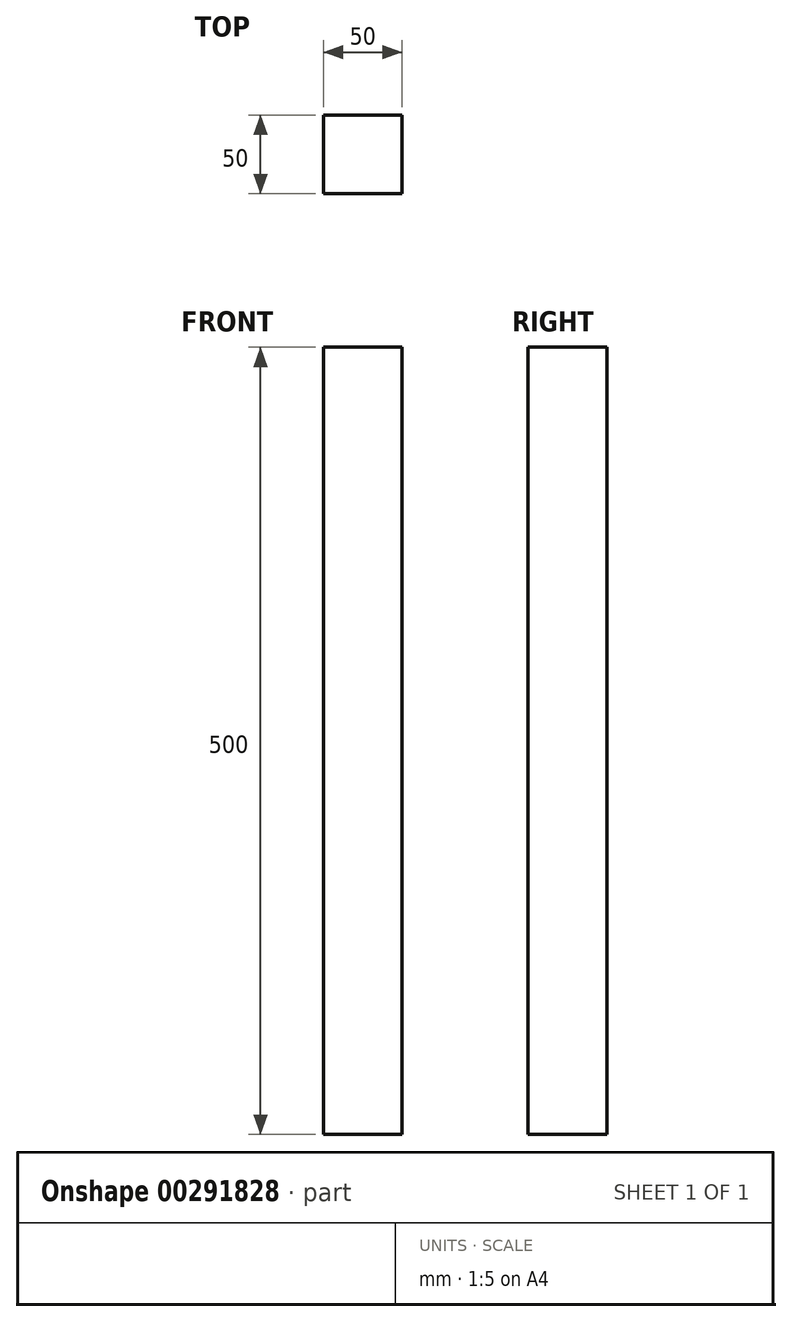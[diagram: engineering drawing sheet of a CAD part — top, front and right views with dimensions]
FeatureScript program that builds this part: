
annotation { "Feature Type Name" : "Feature", "Feature Type Description" : "" }
export const myFeature = defineFeature(function(context is Context, id is Id, definition is map)
    precondition{}
    {
        {
            var Q0;
            Q0=qCreatedBy(makeId("Top.planeOp"),FACE);
            var sketch = newSketch(context, id + "F0", { "sketchPlane" : qUnion([Q0])});
            skLineSegment(sketch, "E0.bottom", {"start": v(-25, -25) * mm, "end": v(25, -25) * mm});
            skLineSegment(sketch, "E0.top", {"start": v(-25, 25) * mm, "end": v(25, 25) * mm});
            skLineSegment(sketch, "E0.left", {"start": v(-25, -25) * mm, "end": v(-25, 25) * mm});
            skLineSegment(sketch, "E0.right", {"start": v(25, -25) * mm, "end": v(25, 25) * mm});
            skPoint(sketch, "E0.middle", {"position": v(0, 0) * mm});
            skSolve(sketch);
        }
        {
            var Q0;
            Q0 = qSketchRegion(id + "F0", true);
            extrude(context, id + "F1", {"entities" : qUnion([Q0]), "depth" : 500 * mm});
        }
    });
